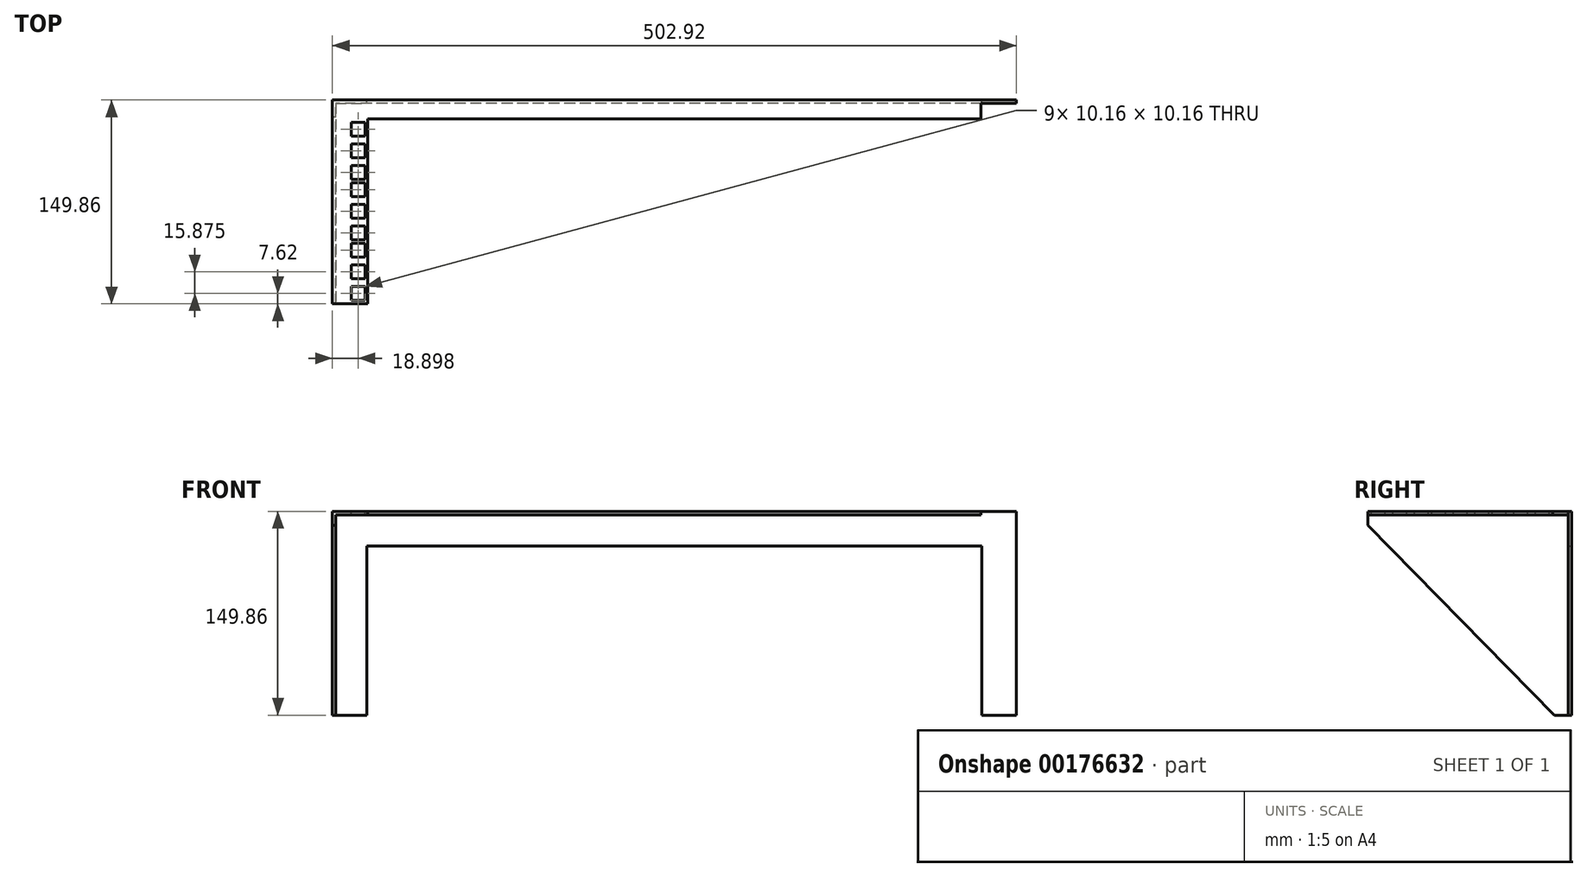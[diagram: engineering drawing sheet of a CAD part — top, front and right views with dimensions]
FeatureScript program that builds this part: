
annotation { "Feature Type Name" : "Feature", "Feature Type Description" : "" }
export const myFeature = defineFeature(function(context is Context, id is Id, definition is map)
    precondition{}
    {
        {
            var Q0;
            Q0=qCreatedBy(makeId("Front.planeOp"),FACE);
            var sketch = newSketch(context, id + "F0", { "sketchPlane" : qUnion([Q0])});
            skLineSegment(sketch, "E0.bottom", {"start": v(226.06, -12.7) * mm, "end": v(-226.06, -12.7) * mm});
            skLineSegment(sketch, "E0.top", {"start": v(251.46, 12.7) * mm, "end": v(-251.46, 12.7) * mm});
            skLineSegment(sketch, "E0.left", {"start": v(251.46, -12.7) * mm, "end": v(251.46, 12.7) * mm});
            skLineSegment(sketch, "E0.right", {"start": v(-251.46, -12.7) * mm, "end": v(-251.46, 12.7) * mm});
            skPoint(sketch, "E0.middle", {"position": v(0, 0) * mm});
            skLineSegment(sketch, "E1.top", {"start": v(-251.46, -137.16) * mm, "end": v(-226.06, -137.16) * mm});
            skLineSegment(sketch, "E1.left", {"start": v(-251.46, -12.7) * mm, "end": v(-251.46, -137.16) * mm});
            skLineSegment(sketch, "E1.right", {"start": v(-226.06, -12.7) * mm, "end": v(-226.06, -137.16) * mm});
            skLineSegment(sketch, "E2.MirrorCS", {"start": v(226.06, -12.7) * mm, "end": v(226.06, -137.16) * mm});
            skLineSegment(sketch, "E3.MirrorCS", {"start": v(251.46, -137.16) * mm, "end": v(226.06, -137.16) * mm});
            skLineSegment(sketch, "E4.MirrorCS", {"start": v(251.46, -12.7) * mm, "end": v(251.46, -137.16) * mm});
            skSolve(sketch);
        }
        {
            var Q0;
            Q0 = qSketchRegion(id + "F0", true);
            extrude(context, id + "F1", {"entities" : qUnion([Q0]), "depth" : 2.54 * mm});
        }
        {
            var Q0;
            Q0=makeQuery(id+"F1.opExtrude","SWEPT_FACE",FACE,{"disambiguationData":[OSD([sQuery(id+"F0.wireOp",EDGE,"E0.right"),sQuery(id+"F0.wireOp",EDGE,"E1.left")])]});
            var sketch = newSketch(context, id + "F2", { "sketchPlane" : qUnion([Q0])});
            skLineSegment(sketch, "E5", {"start": v(2.54, 12.7) * mm, "end": v(149.86, 12.7) * mm});
            skLineSegment(sketch, "E6", {"start": v(149.86, 12.7) * mm, "end": v(149.86, 2.54) * mm});
            skLineSegment(sketch, "E7", {"start": v(149.86, 2.54) * mm, "end": v(12.7, -137.16) * mm});
            skLineSegment(sketch, "E8", {"start": v(12.7, -137.16) * mm, "end": v(2.54, -137.16) * mm});
            skLineSegment(sketch, "E9", {"start": v(2.54, -137.16) * mm, "end": v(2.54, 12.7) * mm});
            skSolve(sketch);
        }
        {
            var Q0;
            Q0 = qSketchRegion(id + "F2", true);
            extrude(context, id + "F3", {"entities" : qUnion([Q0]), "operationType" : NewBodyOperationType.ADD, "oppositeDirection" : true, "depth" : 2.54 * mm});
        }
        {
            var Q0;
            Q0=makeQuery(id+"F3.boolean.opBoolean","MERGE",FACE,{"derivedFrom":[makeQuery(id+"F1.opExtrude","SWEPT_FACE",FACE,{"disambiguationData":[OSD([sQuery(id+"F0.wireOp",EDGE,"E0.top")])]}),makeQuery(id+"F3.opExtrude","SWEPT_FACE",FACE,{"disambiguationData":[OSD([sQuery(id+"F2.wireOp",EDGE,"E5")])]})]});
            var sketch = newSketch(context, id + "F4", { "sketchPlane" : qUnion([Q0])});
            skLineSegment(sketch, "E10.bottom", {"start": v(-248.92, -2.54) * mm, "end": v(-225.43, -2.54) * mm});
            skLineSegment(sketch, "E10.top", {"start": v(-248.92, -149.86) * mm, "end": v(-225.43, -149.86) * mm});
            skLineSegment(sketch, "E10.left", {"start": v(-248.92, -2.54) * mm, "end": v(-248.92, -149.86) * mm});
            skLineSegment(sketch, "E10.right", {"start": v(-225.43, -2.54) * mm, "end": v(-225.43, -149.86) * mm});
            skSolve(sketch);
        }
        {
            var Q0;
            Q0 = qSketchRegion(id + "F4", true);
            extrude(context, id + "F5", {"entities" : qUnion([Q0]), "operationType" : NewBodyOperationType.ADD, "oppositeDirection" : true, "depth" : 2.54 * mm});
        }
        {
            var Q0;
            Q0=makeQuery(id+"F5.boolean.opBoolean","MERGE",FACE,{"derivedFrom":[makeQuery(id+"F3.boolean.opBoolean","MERGE",FACE,{"derivedFrom":[makeQuery(id+"F1.opExtrude","SWEPT_FACE",FACE,{"disambiguationData":[OSD([sQuery(id+"F0.wireOp",EDGE,"E0.top")])]}),makeQuery(id+"F3.opExtrude","SWEPT_FACE",FACE,{"disambiguationData":[OSD([sQuery(id+"F2.wireOp",EDGE,"E5")])]})]}),makeQuery(id+"F5.opExtrude","CAP_FACE",FACE,{"disambiguationData":[OSD([sQuery(id+"F4.wireOp",EDGE,"E10.bottom"),sQuery(id+"F4.wireOp",EDGE,"E10.top"),sQuery(id+"F4.wireOp",EDGE,"E10.left"),sQuery(id+"F4.wireOp",EDGE,"E10.right")])],"isStart":true})]});
            var sketch = newSketch(context, id + "F6", { "sketchPlane" : qUnion([Q0])});
            skLineSegment(sketch, "E11", {"start": v(-232.56, 0) * mm, "end": v(-232.56, -149.86) * mm, "construction": true});
            skPoint(sketch, "E11.endSnap0", {"position": v(-238.44, -149.86) * mm});
            skLineSegment(sketch, "E12.bottom", {"start": v(-227.48, -147.32) * mm, "end": v(-237.64, -147.32) * mm});
            skLineSegment(sketch, "E12.top", {"start": v(-227.48, -137.16) * mm, "end": v(-237.64, -137.16) * mm});
            skLineSegment(sketch, "E12.left", {"start": v(-227.48, -147.32) * mm, "end": v(-227.48, -137.16) * mm});
            skLineSegment(sketch, "E12.right", {"start": v(-237.64, -147.32) * mm, "end": v(-237.64, -137.16) * mm});
            skPoint(sketch, "E12.middle", {"position": v(-232.56, -142.24) * mm});
            skLineSegment(sketch, "E13.1.0.0", {"start": v(-237.64, -131.45) * mm, "end": v(-237.64, -121.29) * mm});
            skLineSegment(sketch, "E13.1.0.1", {"start": v(-227.48, -121.29) * mm, "end": v(-237.64, -121.29) * mm});
            skLineSegment(sketch, "E13.1.0.2", {"start": v(-227.48, -131.45) * mm, "end": v(-227.48, -121.29) * mm});
            skLineSegment(sketch, "E13.1.0.3", {"start": v(-227.48, -131.45) * mm, "end": v(-237.64, -131.45) * mm});
            skLineSegment(sketch, "E13.2.0.0", {"start": v(-237.64, -115.57) * mm, "end": v(-237.64, -105.41) * mm});
            skLineSegment(sketch, "E13.2.0.1", {"start": v(-227.48, -105.41) * mm, "end": v(-237.64, -105.41) * mm});
            skLineSegment(sketch, "E13.2.0.2", {"start": v(-227.48, -115.57) * mm, "end": v(-227.48, -105.41) * mm});
            skLineSegment(sketch, "E13.2.0.3", {"start": v(-227.48, -115.57) * mm, "end": v(-237.64, -115.57) * mm});
            skLineSegment(sketch, "E13.direction1", {"start": v(-237.64, -147.32) * mm, "end": v(-237.64, -131.45) * mm, "construction": true});
            skPoint(sketch, "E14.0.1.0", {"position": v(-232.56, -97.8) * mm});
            skLineSegment(sketch, "E14.0.1.1", {"start": v(-237.64, -102.87) * mm, "end": v(-237.64, -87) * mm, "construction": true});
            skLineSegment(sketch, "E14.0.1.2", {"start": v(-227.48, -102.87) * mm, "end": v(-237.64, -102.87) * mm});
            skLineSegment(sketch, "E14.0.1.3", {"start": v(-227.48, -87) * mm, "end": v(-227.48, -76.84) * mm});
            skPoint(sketch, "E14.0.1.4", {"position": v(-238.44, -105.41) * mm});
            skLineSegment(sketch, "E14.0.1.5", {"start": v(-227.48, -76.84) * mm, "end": v(-237.64, -76.84) * mm});
            skLineSegment(sketch, "E14.0.1.6", {"start": v(-237.64, -87) * mm, "end": v(-237.64, -76.84) * mm});
            skLineSegment(sketch, "E14.0.1.7", {"start": v(-227.48, -71.12) * mm, "end": v(-237.64, -71.12) * mm});
            skLineSegment(sketch, "E14.0.1.8", {"start": v(-227.48, -71.12) * mm, "end": v(-227.48, -60.96) * mm});
            skLineSegment(sketch, "E14.0.1.9", {"start": v(-227.48, -60.96) * mm, "end": v(-237.64, -60.96) * mm});
            skLineSegment(sketch, "E14.0.1.10", {"start": v(-227.48, -102.87) * mm, "end": v(-227.48, -92.71) * mm});
            skLineSegment(sketch, "E14.0.1.11", {"start": v(-227.48, -92.71) * mm, "end": v(-237.64, -92.71) * mm});
            skLineSegment(sketch, "E14.0.1.12", {"start": v(-237.64, -71.12) * mm, "end": v(-237.64, -60.96) * mm});
            skLineSegment(sketch, "E14.0.1.13", {"start": v(-227.48, -87) * mm, "end": v(-237.64, -87) * mm});
            skLineSegment(sketch, "E14.0.1.14", {"start": v(-237.64, -102.87) * mm, "end": v(-237.64, -92.71) * mm});
            skPoint(sketch, "E14.0.2.0", {"position": v(-232.56, -53.34) * mm});
            skLineSegment(sketch, "E14.0.2.1", {"start": v(-237.64, -58.42) * mm, "end": v(-237.64, -42.55) * mm, "construction": true});
            skLineSegment(sketch, "E14.0.2.2", {"start": v(-227.48, -58.42) * mm, "end": v(-237.64, -58.42) * mm});
            skLineSegment(sketch, "E14.0.2.3", {"start": v(-227.48, -42.55) * mm, "end": v(-227.48, -32.39) * mm});
            skPoint(sketch, "E14.0.2.4", {"position": v(-238.44, -60.96) * mm});
            skLineSegment(sketch, "E14.0.2.5", {"start": v(-227.48, -32.39) * mm, "end": v(-237.64, -32.39) * mm});
            skLineSegment(sketch, "E14.0.2.6", {"start": v(-237.64, -42.55) * mm, "end": v(-237.64, -32.39) * mm});
            skLineSegment(sketch, "E14.0.2.7", {"start": v(-227.48, -26.67) * mm, "end": v(-237.64, -26.67) * mm});
            skLineSegment(sketch, "E14.0.2.8", {"start": v(-227.48, -26.67) * mm, "end": v(-227.48, -16.51) * mm});
            skLineSegment(sketch, "E14.0.2.9", {"start": v(-227.48, -16.51) * mm, "end": v(-237.64, -16.51) * mm});
            skLineSegment(sketch, "E14.0.2.10", {"start": v(-227.48, -58.42) * mm, "end": v(-227.48, -48.26) * mm});
            skLineSegment(sketch, "E14.0.2.11", {"start": v(-227.48, -48.26) * mm, "end": v(-237.64, -48.26) * mm});
            skLineSegment(sketch, "E14.0.2.12", {"start": v(-237.64, -26.67) * mm, "end": v(-237.64, -16.51) * mm});
            skLineSegment(sketch, "E14.0.2.13", {"start": v(-227.48, -42.55) * mm, "end": v(-237.64, -42.55) * mm});
            skLineSegment(sketch, "E14.0.2.14", {"start": v(-237.64, -58.42) * mm, "end": v(-237.64, -48.26) * mm});
            skLineSegment(sketch, "E14.direction1", {"start": v(-238.44, -149.86) * mm, "end": v(-213.04, -149.86) * mm, "construction": true});
            skLineSegment(sketch, "E14.direction2", {"start": v(-238.44, -149.86) * mm, "end": v(-238.44, -105.41) * mm, "construction": true});
            skSolve(sketch);
        }
        {
            var Q0;
            Q0 = qSketchRegion(id + "F6", true);
            extrude(context, id + "F7", {"entities" : qUnion([Q0]), "operationType" : NewBodyOperationType.REMOVE, "oppositeDirection" : true, "depth" : 25.4 * mm});
        }
        {
            var Q0;
            {var subQ0=sQuery(id+"F4.wireOp",EDGE,"E10.right");var subQ1=sQuery(id+"F4.wireOp",EDGE,"E10.left");var subQ2=sQuery(id+"F4.wireOp",EDGE,"E10.top");var subQ3=sQuery(id+"F4.wireOp",EDGE,"E10.bottom");var subQ4=sQuery(id+"F2.wireOp",EDGE,"E5");Q0=makeQuery(id+"FEtx3HiDFaFCejL_1.1.F5.boolean.opBoolean","MERGE",FACE,{"derivedFrom":[makeQuery(id+"FEtx3HiDFaFCejL_1.1.F3.boolean.opBoolean","MERGE",FACE,{"derivedFrom":[makeQuery(id+"F5.boolean.opBoolean","MERGE",FACE,{"derivedFrom":[makeQuery(id+"F3.boolean.opBoolean","MERGE",FACE,{"derivedFrom":[makeQuery(id+"F1.opExtrude","SWEPT_FACE",FACE,{"disambiguationData":[OSD([sQuery(id+"F0.wireOp",EDGE,"E0.top")])]}),makeQuery(id+"F3.opExtrude","SWEPT_FACE",FACE,{"disambiguationData":[OSD([subQ4])]})]}),makeQuery(id+"F5.opExtrude","CAP_FACE",FACE,{"disambiguationData":[OSD([subQ3,subQ2,subQ1,subQ0])],"isStart":true})]}),makeQuery(id+"FEtx3HiDFaFCejL_1.1.F3.opExtrude","SWEPT_FACE",FACE,{"disambiguationData":[OSD([subQ4])]})]}),makeQuery(id+"FEtx3HiDFaFCejL_1.1.F5.opExtrude","CAP_FACE",FACE,{"disambiguationData":[OSD([subQ3,subQ2,subQ1,subQ0])],"isStart":true})]});}
            var sketch = newSketch(context, id + "F8", { "sketchPlane" : qUnion([Q0])});
            skLineSegment(sketch, "E15.bottom", {"start": v(-225.43, -2.54) * mm, "end": v(225.43, -2.54) * mm});
            skLineSegment(sketch, "E15.top", {"start": v(-225.43, -13.97) * mm, "end": v(225.43, -13.97) * mm});
            skLineSegment(sketch, "E15.left", {"start": v(-225.43, -2.54) * mm, "end": v(-225.43, -13.97) * mm});
            skLineSegment(sketch, "E15.right", {"start": v(225.43, -2.54) * mm, "end": v(225.43, -13.97) * mm});
            skSolve(sketch);
        }
        {
            var Q0;
            Q0 = qSketchRegion(id + "F8", true);
            extrude(context, id + "F9", {"entities" : qUnion([Q0]), "operationType" : NewBodyOperationType.ADD, "oppositeDirection" : true, "depth" : 2.54 * mm});
        }
        {
            var Q0;
            {var subQ0=sQuery(id+"F4.wireOp",EDGE,"E10.right");var subQ1=sQuery(id+"F4.wireOp",EDGE,"E10.left");var subQ2=sQuery(id+"F4.wireOp",EDGE,"E10.top");var subQ3=sQuery(id+"F4.wireOp",EDGE,"E10.bottom");var subQ4=sQuery(id+"F2.wireOp",EDGE,"E5");Q0=makeQuery(id+"F9.boolean.opBoolean","MERGE",FACE,{"derivedFrom":[makeQuery(id+"FEtx3HiDFaFCejL_1.1.F5.boolean.opBoolean","MERGE",FACE,{"derivedFrom":[makeQuery(id+"FEtx3HiDFaFCejL_1.1.F3.boolean.opBoolean","MERGE",FACE,{"derivedFrom":[makeQuery(id+"F5.boolean.opBoolean","MERGE",FACE,{"derivedFrom":[makeQuery(id+"F3.boolean.opBoolean","MERGE",FACE,{"derivedFrom":[makeQuery(id+"F1.opExtrude","SWEPT_FACE",FACE,{"disambiguationData":[OSD([sQuery(id+"F0.wireOp",EDGE,"E0.top")])]}),makeQuery(id+"F3.opExtrude","SWEPT_FACE",FACE,{"disambiguationData":[OSD([subQ4])]})]}),makeQuery(id+"F5.opExtrude","CAP_FACE",FACE,{"disambiguationData":[OSD([subQ3,subQ2,subQ1,subQ0])],"isStart":true})]}),makeQuery(id+"FEtx3HiDFaFCejL_1.1.F3.opExtrude","SWEPT_FACE",FACE,{"disambiguationData":[OSD([subQ4])]})]}),makeQuery(id+"FEtx3HiDFaFCejL_1.1.F5.opExtrude","CAP_FACE",FACE,{"disambiguationData":[OSD([subQ3,subQ2,subQ1,subQ0])],"isStart":true})]}),makeQuery(id+"F9.opExtrude","CAP_FACE",FACE,{"disambiguationData":[OSD([sQuery(id+"F8.wireOp",EDGE,"E15.bottom"),sQuery(id+"F8.wireOp",EDGE,"E15.top"),sQuery(id+"F8.wireOp",EDGE,"E15.left"),sQuery(id+"F8.wireOp",EDGE,"E15.right")])],"isStart":true})]});}
            var sketch = newSketch(context, id + "F10", { "sketchPlane" : qUnion([Q0])});
            skLineSegment(sketch, "E16", {"start": v(-232.56, -16.51) * mm, "end": v(-232.56, -26.67) * mm, "construction": true});
            skSolve(sketch);
        }
    });
